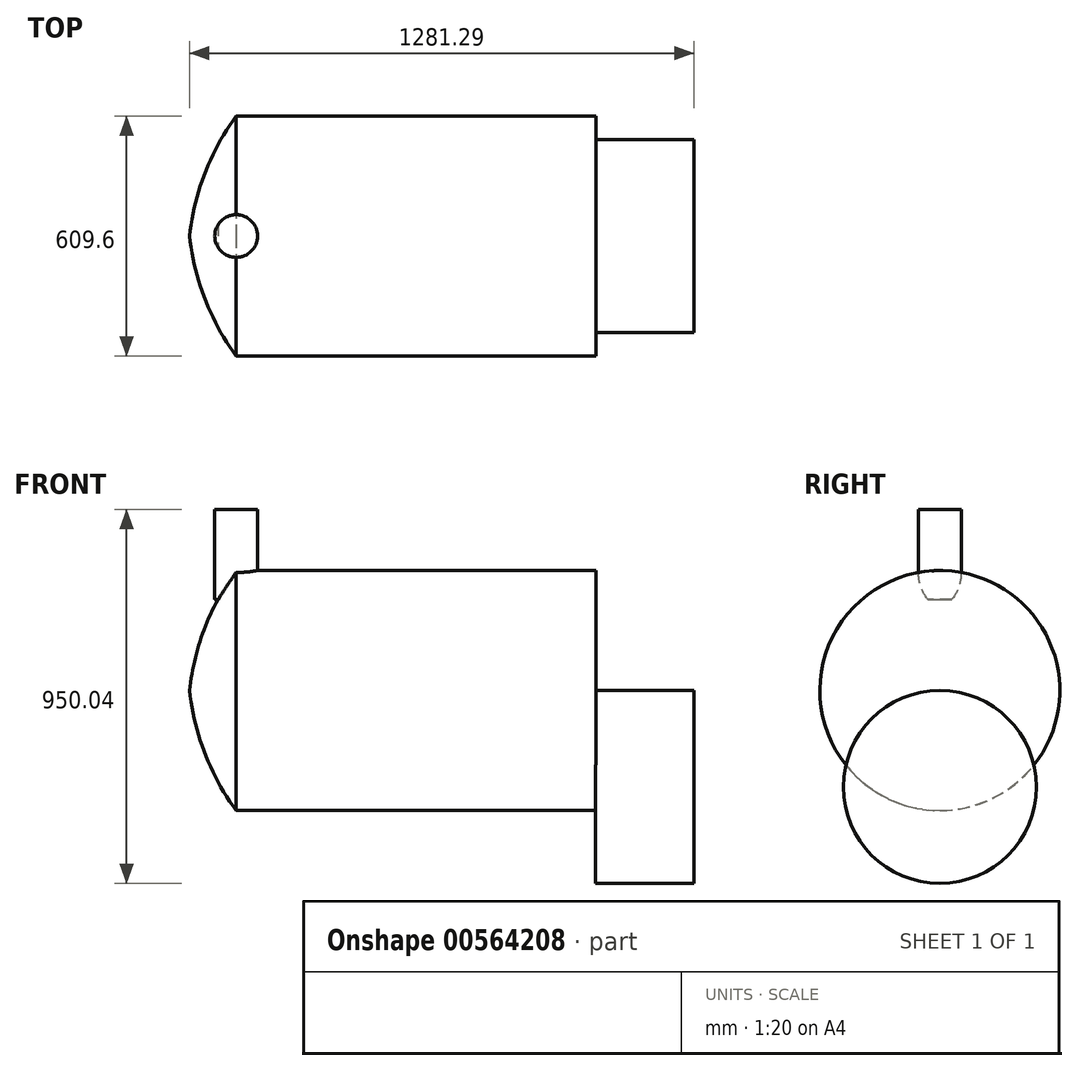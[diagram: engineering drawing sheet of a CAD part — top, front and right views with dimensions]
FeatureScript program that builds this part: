
annotation { "Feature Type Name" : "Feature", "Feature Type Description" : "" }
export const myFeature = defineFeature(function(context is Context, id is Id, definition is map)
    precondition{}
    {
        {
            var Q0;
            Q0=qCreatedBy(makeId("Front.planeOp"),FACE);
            var sketch = newSketch(context, id + "F0", { "sketchPlane" : qUnion([Q0])});
            skLineSegment(sketch, "E0.bottom", {"start": v(0, 0) * mm, "end": v(914.4, 0) * mm});
            skLineSegment(sketch, "E0.top", {"start": v(0, 304.8) * mm, "end": v(914.4, 304.8) * mm});
            skLineSegment(sketch, "E0.left", {"start": v(0, 0) * mm, "end": v(0, 304.8) * mm});
            skLineSegment(sketch, "E0.right", {"start": v(914.4, 0) * mm, "end": v(914.4, 304.8) * mm});
            skLineSegment(sketch, "E1", {"start": v(0, 0) * mm, "end": v(-118.27, 0) * mm});
            skArc(sketch, "E2", {"start": v(0, 304.8) * mm, "mid": v(-79.3, 160.22) * mm, "end": v(-118.27, 0) * mm});
            skSolve(sketch);
        }
        {
            var Q0;
            Q0=makeQuery(id+"F0.imprint","IMPRINT",FACE,{"disambiguationData":[TD([[makeQuery(id+"F0.imprint","IMPRINT",EDGE,{"derivedFrom":sQuery(id+"F0.wireOp",EDGE,"E0.bottom")}),1.0]])]});
            var sketch = newSketch(context, id + "F1", { "sketchPlane" : qUnion([Q0])});
            skLineSegment(sketch, "E3.bottom", {"start": v(912.6, 0) * mm, "end": v(1163.02, 0) * mm});
            skLineSegment(sketch, "E3.top", {"start": v(912.6, -245.06) * mm, "end": v(1163.02, -245.06) * mm});
            skLineSegment(sketch, "E3.left", {"start": v(912.6, 0) * mm, "end": v(912.6, -245.06) * mm});
            skLineSegment(sketch, "E3.right", {"start": v(1163.02, 0) * mm, "end": v(1163.02, -245.06) * mm});
            skSolve(sketch);
        }
        {
            var Q0;
            Q0=qCreatedBy(makeId("Right.planeOp"),FACE);
            var sketch = newSketch(context, id + "F2", { "sketchPlane" : qUnion([Q0])});
            skLineSegment(sketch, "E4.bottom", {"start": v(0, 231.7) * mm, "end": v(54.26, 231.7) * mm});
            skLineSegment(sketch, "E4.top", {"start": v(0, 459.93) * mm, "end": v(54.26, 459.93) * mm});
            skLineSegment(sketch, "E4.left", {"start": v(0, 231.7) * mm, "end": v(0, 459.93) * mm});
            skLineSegment(sketch, "E4.right", {"start": v(54.26, 231.7) * mm, "end": v(54.26, 459.93) * mm});
            skSolve(sketch);
        }
        {
            var Q0;
            Q0=makeQuery(id+"F2.imprint","IMPRINT",FACE,{"disambiguationData":[TD([[makeQuery(id+"F2.imprint","IMPRINT",EDGE,{"derivedFrom":sQuery(id+"F2.wireOp",EDGE,"E4.bottom")}),1.0]])]});
            var Q1;
            Q1=sQuery(id+"F2.wireOp",EDGE,"E4.left");
            revolve(context, id + "F3", {"entities" : qUnion([Q0]), "axis" : qUnion([Q1]), "revolveType" : RevolveType.FULL});
        }
        {
            var Q0;
            Q0=makeQuery(id+"F0.imprint","IMPRINT",FACE,{"disambiguationData":[TD([[makeQuery(id+"F0.imprint","IMPRINT",EDGE,{"derivedFrom":sQuery(id+"F0.wireOp",EDGE,"E0.left")}),1.0]])]});
            var Q1;
            Q1=makeQuery(id+"F0.imprint","IMPRINT",FACE,{"disambiguationData":[TD([[makeQuery(id+"F0.imprint","IMPRINT",EDGE,{"derivedFrom":sQuery(id+"F0.wireOp",EDGE,"E0.bottom")}),1.0]])]});
            var Q2;
            Q2=sQuery(id+"F0.wireOp",EDGE,"E0.bottom");
            revolve(context, id + "F4", {"operationType" : NewBodyOperationType.ADD, "entities" : qUnion([Q0, Q1]), "axis" : qUnion([Q2]), "revolveType" : RevolveType.FULL});
        }
        {
            var Q0;
            Q0 = qSketchRegion(id + "Fjoe1eBUCWAJHtO_1", true);
            var Q1;
            Q1=makeQuery(id+"F1.imprint","IMPRINT",FACE,{"disambiguationData":[TD([[makeQuery(id+"F1.imprint","IMPRINT",EDGE,{"derivedFrom":sQuery(id+"F1.wireOp",EDGE,"E3.top")}),1.0]])]});
            var Q2;
            Q2=sQuery(id+"F1.wireOp",EDGE,"E3.top");
            revolve(context, id + "F5", {"operationType" : NewBodyOperationType.ADD, "entities" : qUnion([Q0, Q1]), "axis" : qUnion([Q2]), "revolveType" : RevolveType.FULL});
        }
    });
